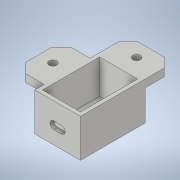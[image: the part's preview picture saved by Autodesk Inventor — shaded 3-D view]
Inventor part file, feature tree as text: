
AUTODESK INVENTOR PART (.ipt)
format: ipt  version: 2022 (Build 260153000, 153)  size: 207,360 bytes
history: native  units: mm
features: extrude x7, sketch x7, other x1, shell x1, chamfer x1
ambient origin geometry x8: Origin, YZ Plane, XZ Plane, XY Plane, X Axis, Y Axis, Z Axis, Center Point
bodies: Body1 (feature_tree)
feature tree (17):
  other  "Sólido1"
  extrude  "Extrusão1"  Depth=34.0mm
  shell  "Casca1"  Thickness=20.0mm
  extrude  "Extrusão2"  Depth=2.0mm
  extrude  "Extrusão5"  Depth=5.0mm
  extrude  "Extrusão6"  Depth=3.0mm
  extrude  "Extrusão8"  Depth=3.0mm
  chamfer  "Chanfro3"  Distance=30.0mm
  extrude  "Extrusão9"  Depth=4.0mm
  extrude  "Extrusão11"  Depth=4.0mm
  sketch  "Esboço1"  dims[d0=24.0mm d1=34.0mm d2=20.0mm d3=0.0mm]
  sketch  "Esboço2"  dims[d4=2.0mm d5=12.0mm]
  sketch  "Esboço5"  dims[d6=17.0mm d7=5.0mm]
  sketch  "Esboço6"  dims[d8=3.0mm d9=2.5mm]
  sketch  "Esboço8"  dims[d10=2.5mm d11=3.0mm]
  sketch  "Esboço9"  dims[d12=2.5mm d13=30.0mm d14=0.0mm]
  sketch  "Esboço11"  dims[d32=3.7mm d33=3.7mm d34=6.0mm d35=6.0mm d36=0.8mm d37=0.0mm d38=8.2mm d39=12.0mm d40=17.0mm d41=5.0mm d42=9.0mm d43=2.0mm d44=0.0mm d57=15.0mm d58=15.0mm d59=24.0mm d60=5.0mm d61=4.0mm d62=0.0mm d63=5.0mm d64=2.0mm d65=45.0deg d66=4.0mm d67=4.0mm d68=7.5mm d69=7.5mm d70=4.0mm d71=0.0mm d79=4.0mm d80=9.0mm d81=10.0mm d82=4.0mm d83=10.0mm d84=4.0mm d85=0.0mm]
